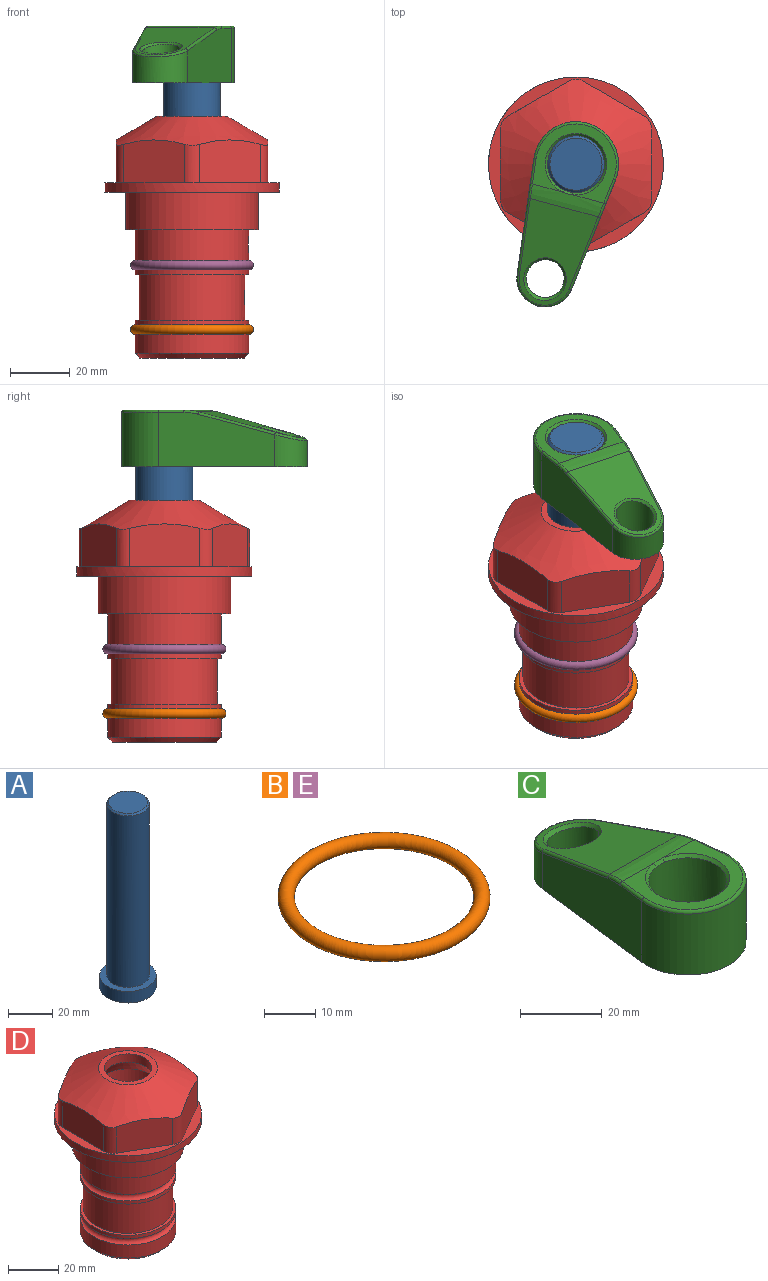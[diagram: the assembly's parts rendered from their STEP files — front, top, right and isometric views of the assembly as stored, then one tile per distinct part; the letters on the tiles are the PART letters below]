
ASSEMBLY  parts=5 mates=4
PART A: 6 faces, bbox 25.4x25.4x101.6 mm
  f0: plane 17.46x17.46mm, normal (0,0,1), area 239.5mm2, adj f5
  f1: plane 25.4x25.4mm, normal (0,0,-1), area 506.7mm2, adj f2
  f2: cylinder r=12.7mm len=25.4mm, axis (0,0,1), area 506.7mm2, adj f1,f3
  f3: plane 25.4x25.4mm, normal (0,0,1), area 221.7mm2, adj f2,f4
  f4: cylinder r=9.53mm len=94.46mm, axis (0,0,1), area 5653mm2, adj f3,f5
  f5: cone r=8.73mm half-angle=45deg, axis (0,0,-1), area 64.4mm2, adj f0,f4
PART B: 1 faces, bbox 44.7x44.7x3.2 mm
  f0: torus R=19.05mm, axis (0,0,1), area 1193.9mm2
PART C: 31 faces, bbox 31.7x65.5x19.8 mm
  f0: plane 39.12x18.26mm, normal (0.99,0.12,0), area 612.2mm2, adj f1,f4,f7,f11,f13,f15
  f1: cylinder r=9.53mm len=18.91mm, axis (0,0,-1), area 296.1mm2, adj f0,f2,f7,f17
  f2: plane 39.12x18.26mm, normal (-0.99,0.12,0), area 612.2mm2, adj f1,f4,f7,f12,f14,f16
  f3: cylinder r=6.35mm len=12.7mm, axis (0,0,-1), area 362.4mm2, adj f7,f18
  f4: cylinder r=14.29mm len=28.58mm, axis (0,0,-1), area 882.2mm2, adj f0,f2,f7,f10
  f5: cylinder r=9.53mm len=19.05mm, axis (0,0,-1), area 1092.6mm2, adj f7,f19,f20
  f6: plane 26.99x23.69mm, normal (0,0,1), area 216.2mm2, adj f9,f10,f11,f12,f19
  f7: plane 63.5x28.58mm, normal (0,0,-1), area 661.8mm2, adj f0,f1,f2,f3,f4,f5,f22,f23
  f8: plane 33.52x23.6mm, normal (0,0.26,0.97), area 486mm2, adj f9,f15,f16,f17,f18
  f9: cylinder r=19.05mm len=24.72mm, axis (1,0,0), area 120.4mm2, adj f6,f8,f13,f14,f20
  f10: torus R=13.49mm, axis (0,0,1), area 59mm2, adj f4,f6,f11,f12
  f11: cylinder r=0.79mm len=8.67mm, axis (0.12,-0.99,0), area 10.8mm2, adj f0,f6,f10,f13
  f12: cylinder r=0.79mm len=8.67mm, axis (0.12,0.99,0), area 10.8mm2, adj f2,f6,f10,f14
  f13: bspline ~4.95x1.42mm, area 6.1mm2, adj f0,f9,f11,f15
  f14: bspline ~4.95x1.42mm, area 6.1mm2, adj f2,f9,f12,f16
  f15: cylinder r=0.79mm len=25.95mm, axis (0.12,-0.96,0.26), area 32.9mm2, adj f0,f8,f13,f17
  f16: cylinder r=0.79mm len=25.95mm, axis (0.12,0.96,-0.26), area 32.9mm2, adj f2,f8,f14,f17
  f17: bspline ~18.91x8.38mm, area 30mm2, adj f1,f8,f15,f16
  f18: bspline ~14.29x14.29mm, area 48.3mm2, adj f3,f8
  f19: cone r=9.53mm half-angle=45deg, axis (0,0,1), area 66.5mm2, adj f5,f6,f20
  f20: bspline ~3.22x0.96mm, area 3.5mm2, adj f5,f9,f19
  f21: plane 2.75x2.72mm, normal (0,0,-1), area 2.9mm2, adj f23,f25,f28
  f22: plane 23.05x15.88mm, normal (-0.99,-0.12,0), area 323.6mm2, adj f7,f25,f26,f27,f28,f29
  f23: plane 23.05x15.88mm, normal (0.99,-0.12,0), area 323.6mm2, adj f7,f21,f25,f27,f28,f30
  f24: cylinder r=9.53mm len=10.69mm, axis (0,0,-1), area 114.7mm2, adj f7,f27,f29,f30
  f25: cylinder r=12.7mm len=20.59mm, axis (0,0,-1), area 381.1mm2, adj f7,f21,f22,f23,f26,f28
  f26: plane 2.75x2.72mm, normal (0,0,-1), area 2.9mm2, adj f22,f25,f28
  f27: plane 19.72x18.37mm, normal (0,-0.26,-0.97), area 291.8mm2, adj f22,f23,f24,f28,f29,f30
  f28: cylinder r=15.88mm len=19.92mm, axis (1,0,0), area 54.8mm2, adj f21,f22,f23,f25,f26,f27
  f29: cylinder r=1.59mm len=11mm, axis (0,0,-1), area 34.7mm2, adj f7,f22,f24,f27
  f30: cylinder r=1.59mm len=11mm, axis (0,0,-1), area 34.7mm2, adj f7,f23,f24,f27
PART D: 36 faces, bbox 58.7x58.7x81 mm
  f0: cylinder r=17.78mm len=35.56mm, axis (0,0,1), area 1670.8mm2, adj f23,f24,f31
  f1: cylinder r=19.05mm len=38.1mm, axis (0,0,1), area 1191.9mm2, adj f26,f27,f30
  f2: plane 58.66x58.66mm, normal (0,0,-1), area 1150.6mm2, adj f3,f28
  f3: cylinder r=29.33mm len=58.66mm, axis (0,0,-1), area 585.1mm2, adj f2,f4
  f4: plane 58.66x58.66mm, normal (0,0,1), area 475.9mm2, adj f3,f5,f6,f7,f8,f9,f10,f11
  f5: plane 20.32x14.34mm, normal (-0.5,0.87,0), area 324.4mm2, adj f4,f15,f16,f17
  f6: plane 20.32x14.34mm, normal (0.5,0.87,0), area 324.4mm2, adj f4,f14,f15,f17
  f7: plane 23.48x14.34mm, normal (1,0,0), area 324.4mm2, adj f4,f13,f14,f17
  f8: plane 20.32x14.34mm, normal (0.5,-0.87,0), area 324.4mm2, adj f4,f12,f13,f17
  f9: plane 20.32x14.34mm, normal (-0.5,-0.87,0), area 324.4mm2, adj f4,f11,f12,f17
  f10: plane 23.48x14.34mm, normal (-1,0,0), area 324.4mm2, adj f4,f11,f16,f17
  f11: cylinder r=5.08mm len=12.85mm, axis (0,0,-1), area 67.2mm2, adj f4,f9,f10,f17
  f12: cylinder r=5.08mm len=12.85mm, axis (0,0,-1), area 67.2mm2, adj f4,f8,f9,f17
  f13: cylinder r=5.08mm len=12.85mm, axis (0,0,-1), area 67.2mm2, adj f4,f7,f8,f17
  f14: cylinder r=5.08mm len=12.85mm, axis (0,0,-1), area 67.2mm2, adj f4,f6,f7,f17
  f15: cylinder r=5.08mm len=12.85mm, axis (0,0,-1), area 67.2mm2, adj f4,f5,f6,f17
  f16: cylinder r=5.08mm len=12.85mm, axis (0,0,-1), area 67.2mm2, adj f4,f5,f10,f17
  f17: cone r=11.73mm half-angle=60deg, axis (0,0,-1), area 2071.8mm2, adj f5,f6,f7,f8,f9,f10,f11,f12
  f18: plane 23.46x23.46mm, normal (0,0,1), area 147.4mm2, adj f17,f35
  f19: plane 34.93x34.93mm, normal (0,0,-1), area 958mm2, adj f29
  f20: cylinder r=19.05mm len=38.1mm, axis (0,0,1), area 760.1mm2, adj f21,f29
  f21: torus R=19.05mm, axis (0,0,1), area 565.3mm2, adj f20,f22
  f22: cylinder r=19.05mm len=38.1mm, axis (0,0,1), area 190mm2, adj f21,f23
  f23: plane 38.1x38.1mm, normal (0,0,1), area 146.9mm2, adj f0,f22
  f24: plane 38.1x38.1mm, normal (0,0,-1), area 146.9mm2, adj f0,f25
  f25: cylinder r=19.05mm len=38.1mm, axis (0,0,1), area 190mm2, adj f24,f26
  f26: torus R=19.05mm, axis (0,0,1), area 565.3mm2, adj f1,f25
  f27: plane 44.45x44.45mm, normal (0,0,-1), area 411.7mm2, adj f1,f28
  f28: cylinder r=22.23mm len=44.45mm, axis (0,0,1), area 1773.5mm2, adj f2,f27
  f29: cone r=19.05mm half-angle=45deg, axis (0,0,1), area 257.5mm2, adj f19,f20
  f30: cylinder r=3.17mm len=6.75mm, axis (-1,0,0), area 128mm2, adj f1,f33
  f31: cylinder r=3.17mm len=6.35mm, axis (-1,0,0), area 102.5mm2, adj f0,f33
  f32: plane 25.4x25.4mm, normal (0,0,1), area 506.7mm2, adj f33
  f33: cylinder r=12.7mm len=66.42mm, axis (0,0,-1), area 5236.2mm2, adj f30,f31,f32,f34
  f34: cone r=9.53mm half-angle=30deg, axis (0,0,-1), area 443.4mm2, adj f33,f35
  f35: cylinder r=9.53mm len=19.05mm, axis (0,0,-1), area 240.9mm2, adj f18,f34
PART E: same geometry as B
PLACE A rot(axis=(0,0,1),164.9deg) t=(0,0,-7.8)mm
PLACE B t=(0,0,-21.59)mm
PLACE C rot(axis=(0,0,1),164.9deg) t=(0,0,-7.8)mm
PLACE D at identity fixed
PLACE E at identity
MATE fastened E.f0 <-> D.f0  axis (0,0,1) through (0,0,-24.51)mm
MATE fastened C.f4 <-> A.f2  axis (0,0,1) through (0,0,55.7)mm
MATE cylindrical A.f2 <-> D.f0  axis (0,0,-1) through (0,0,-45.9)mm
MATE fastened B.f0 <-> D.f0  axis (0,0,1) through (0,0,-46.1)mm
